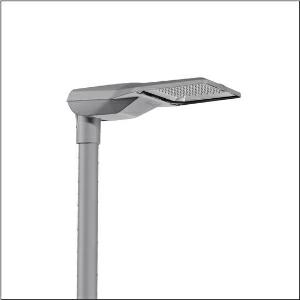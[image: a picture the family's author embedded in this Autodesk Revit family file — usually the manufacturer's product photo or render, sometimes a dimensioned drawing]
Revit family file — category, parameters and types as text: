
# Revit family: streetlight_sl_21_iq_midi___st0_8a_5xe3c41g08mb_fe6c
name_source: partatom
category: Lighting Fixtures
units: mm (PartAtom-declared; Revit-internal decimal feet)

## family parameters
Cut with Voids When Loaded = No
Host = Face
Light Source = No
Part Type = Normal
Room Calculation Point = No
Round Connector Dimension = Use Diameter
Shared = No

## types (1)
- --- (1 x LED, 20360 lm, 146.7 W, 4000K)
    Apparent Load = 147 VA
    CIE Flux Codes = 38 75 97 100 100
    Color Rendering = 70
    Color Temperature = 4000K
    Default Elevation = 1800 mm
    Description = Streetlight SL 21 iQ midi, mast luminaire, primary light control with lens, of PMMA, primary optical cover: cover, of toughened safety glass, transparent, light distribution: ST0.8a, light emission: direct distribution, primary light characteristic: asymmetric, installation type: post-top, side-entry, LED, High Power LED, rated luminous flux: 20.360lm, luminous efficacy: 139lm/W, light colour: 740, colour temperature: 4000K, control: Street-Remote, Auto-Match, Temp-Guard, Lumen-Switch, Night-Set, Smart-Wire, Light-Fading, Desk-Remote (wireless, voltage-free reading and setting of iQ features in the workshop via application-optimized NFC function/RFID function), optimised constant luminous flux control (CLO 2.0), presetting dimming linear, mains connection: 230..240V, AC, 50/60Hz, start of lifetime: 147W, end of service life: 161W, reduction: 62W, luminaire housing, of diecast aluminium, powder-coated, Siteco® metallic grey (DB 702S), corrosivity category C5 mid according to DIN EN ISO 12944, please order mast flange separately, inclination adjustable: 0°, 5°, 10°, 15°, sealing non-destructively replaceable, multi-level sealing system, length: 644mm, width: 335mm, height: 110mm, mast flange for spigot size: 42mm (side-entry): 5XC10008XM4, 60/48mm (side-entry/post-top): 5XC10108XM2, 76/60mm (side-entry/post-top): 5XC10108XM1, protection rating (complete): IP66, insulation class (complete): insulation class II (safety insulation), certification: CE, ENEC, ENEC+, VDE, impact resistance: IK09, permissible operating ambient temperature for outdoor applications: -40..+50°C, standard-compliant lighting for roads and squares, packaging unit: 1 piece

Light Distribution: ST0.8a
    Height = 111 mm
    Lamp = 1 x LED
    Lamp Light Flux = 20360 lm
    Lamp Power = 146.7 W
    Lamp count = 1
    Length = 644 mm
    Luminous efficacy = 139 lm/W
    Manufacturer = Siteco
    ModVariant = No
    Model = 5XE3C41G08MB
    Number of Poles = 1
    OnlyDefault = Yes
    Power Factor = 1
    Product Name = Streetlight SL 21 iQ midi | ST0.8a
    Product group = mast luminaire | pylon top
    ProductGroupID = 6100
    Protection Class = Protection class II
    Protection Degree = IP 66
    RLX_Detail_Level = 1
    RLX_Emergency_Light_Flux = 0 lm
    RLX_Emergency_Type = 0
    RLX_Emergency_Type_DB = No
    RlxData = <blob elided: 90865 chars, md5=3978ce30>
    Socket = socket
    Standby Power = 0 W
    System Light Flux = 20360 lm
    System Power = 147 W
    Type Comments = factory setting: luminous flux: 100 % | dim-lin: 254 | 753 mA
    Type Image = l_1004298.jpg
    URL = http://relux.com
    VarID = @adj_119641
    Voltage = 0 V
    Weight = 0.00 kg
    Width = 336 mm

## geometry (parser evidence)
native form markers: Blend x4, Sweep x13
no freeform markers — native parametric forms only
